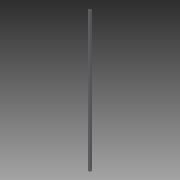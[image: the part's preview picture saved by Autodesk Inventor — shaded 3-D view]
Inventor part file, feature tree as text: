
AUTODESK INVENTOR PART (.ipt)
format: ipt  version: 2015 SP1 (Build 190203100, 203)  size: 81,408 bytes
history: native  units: mm
features: other x3, sketch x3
ambient origin geometry x8: Origin, YZ Plane, XZ Plane, XY Plane, X Axis, Y Axis, Z Axis, Center Point
bodies: Solid1 (feature_tree)
feature tree (6):
  other  "Pied.ipt"
  other  "Solid1::Pied.ipt"
  other  "TaggingFeature1"
  sketch  "Sketch1"  dims[d0=10.0mm]
  sketch  "Sketch2"
  sketch  "Sketch3"
